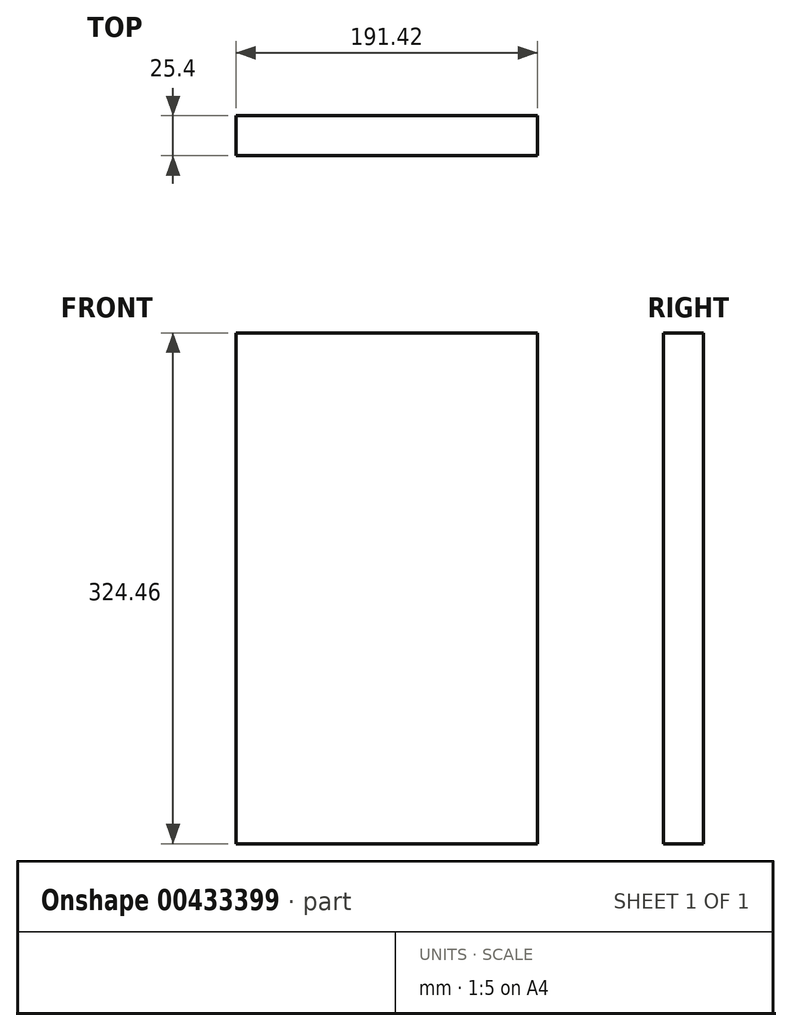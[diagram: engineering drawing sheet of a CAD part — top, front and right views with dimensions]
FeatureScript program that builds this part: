
annotation { "Feature Type Name" : "Feature", "Feature Type Description" : "" }
export const myFeature = defineFeature(function(context is Context, id is Id, definition is map)
    precondition{}
    {
        {
            var Q0;
            Q0=qCreatedBy(makeId("Front.planeOp"),FACE);
            var sketch = newSketch(context, id + "F0", { "sketchPlane" : qUnion([Q0])});
            skLineSegment(sketch, "E0.bottom", {"start": v(-95.71, 162.23) * mm, "end": v(95.71, 162.23) * mm});
            skLineSegment(sketch, "E0.top", {"start": v(-95.71, -162.23) * mm, "end": v(95.71, -162.23) * mm});
            skLineSegment(sketch, "E0.left", {"start": v(-95.71, 162.23) * mm, "end": v(-95.71, -162.23) * mm});
            skLineSegment(sketch, "E0.right", {"start": v(95.71, 162.23) * mm, "end": v(95.71, -162.23) * mm});
            skPoint(sketch, "E0.middle", {"position": v(0, 0) * mm});
            skSolve(sketch);
        }
        {
            var Q0;
            Q0 = qSketchRegion(id + "F0", true);
            extrude(context, id + "F1", {"entities" : qUnion([Q0]), "depth" : 25.4 * mm});
        }
    });
